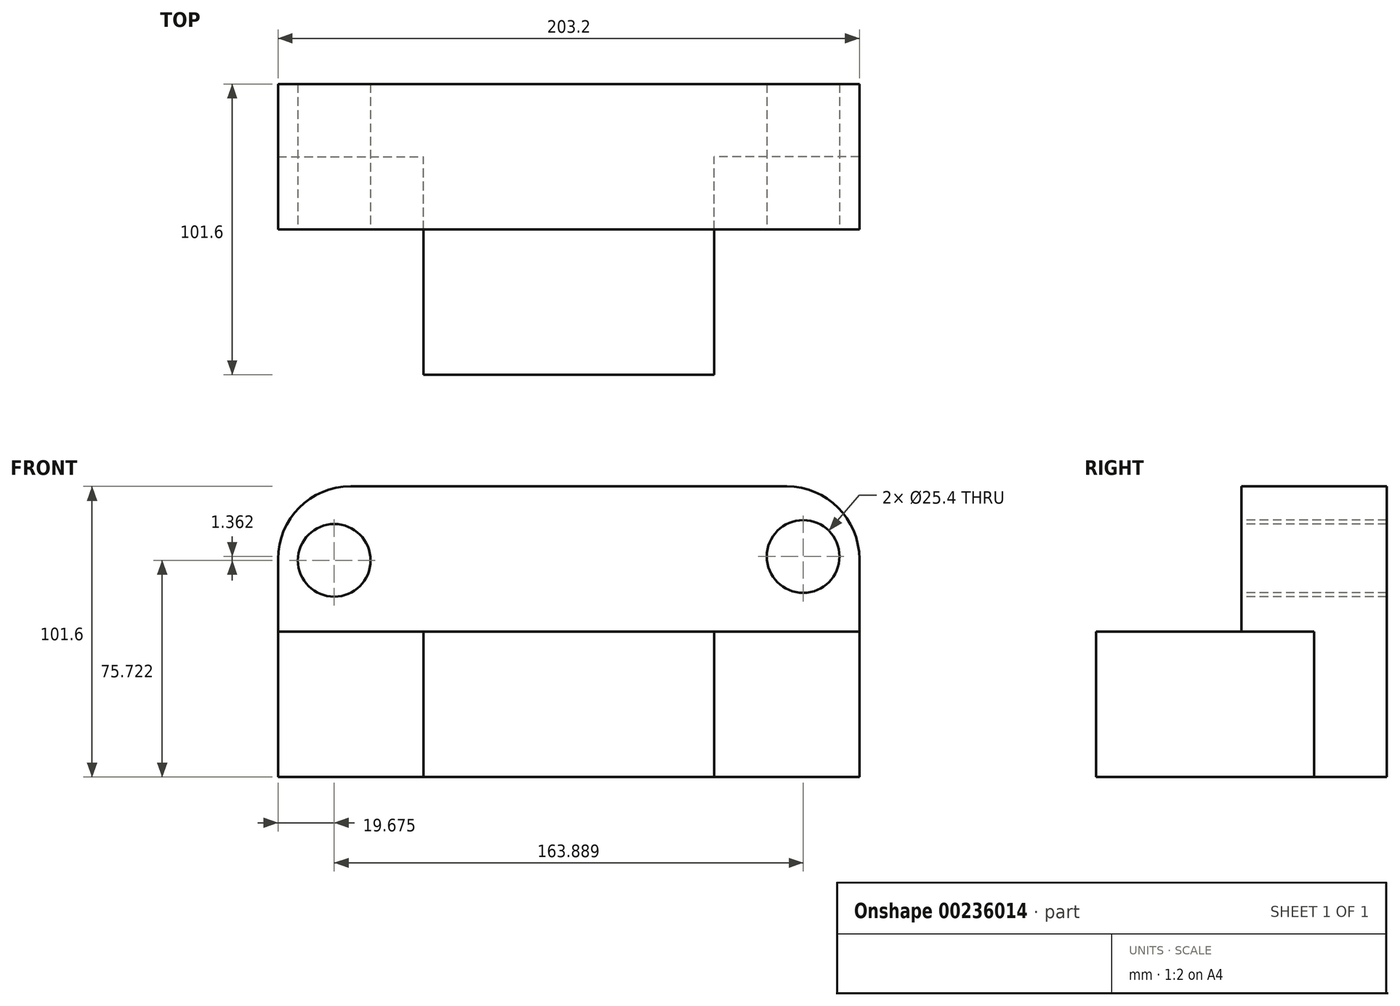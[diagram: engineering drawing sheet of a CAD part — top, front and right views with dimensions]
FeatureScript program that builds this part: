
annotation { "Feature Type Name" : "Feature", "Feature Type Description" : "" }
export const myFeature = defineFeature(function(context is Context, id is Id, definition is map)
    precondition{}
    {
        {
            var Q0;
            Q0=qCreatedBy(makeId("Top.planeOp"),FACE);
            var sketch = newSketch(context, id + "F0", { "sketchPlane" : qUnion([Q0])});
            skLineSegment(sketch, "E0.bottom", {"start": v(-89.89, -22.82) * mm, "end": v(11.71, -22.82) * mm});
            skLineSegment(sketch, "E0.top", {"start": v(-89.89, 78.78) * mm, "end": v(11.71, 78.78) * mm});
            skLineSegment(sketch, "E0.left", {"start": v(-89.89, -22.82) * mm, "end": v(-89.89, 78.78) * mm});
            skLineSegment(sketch, "E0.right", {"start": v(11.71, -22.82) * mm, "end": v(11.71, 78.78) * mm});
            skSolve(sketch);
        }
        {
            var Q0;
            Q0=makeQuery(id+"F0.imprint","IMPRINT",FACE,{"disambiguationData":[TD([[makeQuery(id+"F0.imprint","IMPRINT",EDGE,{"derivedFrom":sQuery(id+"F0.wireOp",EDGE,"E0.bottom")}),1.0]])]});
            extrude(context, id + "F1", {"entities" : qUnion([Q0]), "depth" : 50.8 * mm});
        }
        {
            var Q0;
            Q0=makeQuery(id+"F1.opExtrude","SWEPT_FACE",FACE,{"disambiguationData":[OSD([sQuery(id+"F0.wireOp",EDGE,"E0.right")])]});
            var sketch = newSketch(context, id + "F2", { "sketchPlane" : qUnion([Q0])});
            skLineSegment(sketch, "E1", {"start": v(78.78, 50.8) * mm, "end": v(53.38, 50.8) * mm});
            skLineSegment(sketch, "E2", {"start": v(53.38, 50.8) * mm, "end": v(53.38, 0) * mm});
            skSolve(sketch);
        }
        {
            var Q0;
            Q0=makeQuery(id+"F2.imprint","IMPRINT",FACE,{"disambiguationData":[TD([[makeQuery(id+"F2.imprint","IMPRINT",EDGE,{"derivedFrom":sQuery(id+"F2.wireOp",EDGE,"E1")}),-1.0]])]});
            extrude(context, id + "F3", {"entities" : qUnion([Q0]), "operationType" : NewBodyOperationType.ADD, "depth" : 50.8 * mm});
        }
        {
            var Q0;
            Q0=makeQuery(id+"F1.opExtrude","SWEPT_FACE",FACE,{"disambiguationData":[OSD([sQuery(id+"F0.wireOp",EDGE,"E0.left")])]});
            var sketch = newSketch(context, id + "F4", { "sketchPlane" : qUnion([Q0])});
            skLineSegment(sketch, "E3", {"start": v(-78.78, 50.8) * mm, "end": v(-53.38, 50.8) * mm});
            skLineSegment(sketch, "E4", {"start": v(-53.38, 50.8) * mm, "end": v(-53.38, 0) * mm});
            skSolve(sketch);
        }
        {
            var Q0;
            Q0=makeQuery(id+"F4.imprint","IMPRINT",FACE,{"disambiguationData":[TD([[makeQuery(id+"F4.imprint","IMPRINT",EDGE,{"derivedFrom":sQuery(id+"F4.wireOp",EDGE,"E3")}),1.0]])]});
            extrude(context, id + "F5", {"entities" : qUnion([Q0]), "operationType" : NewBodyOperationType.ADD, "depth" : 50.8 * mm});
        }
        {
            var Q0;
            Q0=makeQuery(id+"F5.boolean.opBoolean","MERGE",FACE,{"derivedFrom":[makeQuery(id+"F3.boolean.opBoolean","MERGE",FACE,{"derivedFrom":[makeQuery(id+"F1.opExtrude","CAP_FACE",FACE,{"disambiguationData":[OSD([sQuery(id+"F0.wireOp",EDGE,"E0.bottom"),sQuery(id+"F0.wireOp",EDGE,"E0.top"),sQuery(id+"F0.wireOp",EDGE,"E0.left"),sQuery(id+"F0.wireOp",EDGE,"E0.right")])],"isStart":false}),makeQuery(id+"F3.opExtrude","SWEPT_FACE",FACE,{"disambiguationData":[OSD([sQuery(id+"F2.wireOp",EDGE,"E1")])]})]}),makeQuery(id+"F5.opExtrude","SWEPT_FACE",FACE,{"disambiguationData":[OSD([sQuery(id+"F4.wireOp",EDGE,"E3")])]})]});
            var sketch = newSketch(context, id + "F6", { "sketchPlane" : qUnion([Q0])});
            skLineSegment(sketch, "E5", {"start": v(-89.89, 53.38) * mm, "end": v(11.71, 53.38) * mm});
            skSolve(sketch);
        }
        {
            var Q0;
            Q0=makeQuery(id+"F6.imprint","IMPRINT",FACE,{"disambiguationData":[TD([[makeQuery(id+"F6.imprint","IMPRINT",EDGE,{"derivedFrom":sQuery(id+"F6.wireOp",EDGE,"E5")}),1.0]])]});
            extrude(context, id + "F7", {"entities" : qUnion([Q0]), "operationType" : NewBodyOperationType.ADD, "depth" : 25.4 * mm});
        }
        {
            var Q0;
            Q0=makeQuery(id+"F7.opExtrude","CAP_FACE",FACE,{"disambiguationData":[OSD([sQuery(id+"F0.wireOp",EDGE,"E0.top"),sQuery(id+"F0.wireOp",EDGE,"E0.left"),sQuery(id+"F0.wireOp",EDGE,"E0.right"),sQuery(id+"F2.wireOp",EDGE,"E1"),sQuery(id+"F2.wireOp",EDGE,"E2"),sQuery(id+"F4.wireOp",EDGE,"E3"),sQuery(id+"F4.wireOp",EDGE,"E4"),sQuery(id+"F6.wireOp",EDGE,"E5")])],"isStart":false});
            extrude(context, id + "F8", {"entities" : qUnion([Q0]), "operationType" : NewBodyOperationType.ADD, "depth" : 25.4 * mm});
        }
        {
            var Q0;
            {var subQ0=sQuery(id+"F6.wireOp",EDGE,"E5");var subQ1=sQuery(id+"F4.wireOp",EDGE,"E4");var subQ2=sQuery(id+"F4.wireOp",EDGE,"E3");var subQ3=sQuery(id+"F2.wireOp",EDGE,"E2");var subQ4=sQuery(id+"F2.wireOp",EDGE,"E1");var subQ5=sQuery(id+"F0.wireOp",EDGE,"E0.right");var subQ6=sQuery(id+"F0.wireOp",EDGE,"E0.left");Q0=makeQuery(id+"F8.boolean.opBoolean","MERGE",FACE,{"derivedFrom":[makeQuery(id+"F7.boolean.opBoolean","MERGE",FACE,{"derivedFrom":[makeQuery(id+"F3.opExtrude","SWEPT_FACE",FACE,{"disambiguationData":[OSD([subQ3])]}),makeQuery(id+"F5.opExtrude","SWEPT_FACE",FACE,{"disambiguationData":[OSD([subQ1])]}),makeQuery(id+"F7.opExtrude","SWEPT_FACE",FACE,{"disambiguationData":[OSD([subQ6,subQ5,subQ4,subQ3,subQ2,subQ1,subQ0])]})]}),makeQuery(id+"F8.opExtrude","SWEPT_FACE",FACE,{"disambiguationData":[OSD([subQ6,subQ5,subQ4,subQ3,subQ2,subQ1,subQ0])]})]});}
            var sketch = newSketch(context, id + "F9", { "sketchPlane" : qUnion([Q0])});
            skLineSegment(sketch, "E6", {"start": v(-89.89, 50.8) * mm, "end": v(-140.69, 50.8) * mm});
            skLineSegment(sketch, "E7", {"start": v(11.71, 50.8) * mm, "end": v(62.51, 50.8) * mm});
            skSolve(sketch);
        }
        {
            var Q0;
            {var subQ9=sQuery(id+"F9.wireOp",EDGE,"E6");Q0=makeQuery(id+"F9.imprint","IMPRINT",FACE,{"disambiguationData":[TD([[makeQuery(id+"F9.imprint","IMPRINT",EDGE,{"derivedFrom":subQ9}),-1.0]])]});}
            extrude(context, id + "F10", {"entities" : qUnion([Q0]), "operationType" : NewBodyOperationType.ADD, "depth" : 25.4 * mm});
        }
        {
            var Q0;
            Q0=makeQuery(id+"F10.opExtrude","CAP_FACE",FACE,{"disambiguationData":[OSD([sQuery(id+"F0.wireOp",EDGE,"E0.left"),sQuery(id+"F0.wireOp",EDGE,"E0.right"),sQuery(id+"F2.wireOp",EDGE,"E1"),sQuery(id+"F2.wireOp",EDGE,"E2"),sQuery(id+"F4.wireOp",EDGE,"E3"),sQuery(id+"F4.wireOp",EDGE,"E4"),sQuery(id+"F6.wireOp",EDGE,"E5"),sQuery(id+"F9.wireOp",EDGE,"E6"),sQuery(id+"F9.wireOp",EDGE,"E7")])],"isStart":false});
            var sketch = newSketch(context, id + "F11", { "sketchPlane" : qUnion([Q0])});
            skCircle(sketch, "E8", {"center": v(31.18, 80.79) * mm, "radius": 12.7 * mm});
            skCircle(sketch, "E9", {"center": v(-121.02, 75.72) * mm, "radius": 12.7 * mm});
            skSolve(sketch);
        }
        {
            var Q0;
            Q0=makeQuery(id+"F11.imprint","IMPRINT",FACE,{"disambiguationData":[TD([[makeQuery(id+"F11.imprint","IMPRINT",EDGE,{"derivedFrom":sQuery(id+"F11.wireOp",EDGE,"E9")}),1.0]])]});
            extrude(context, id + "F12", {"entities" : qUnion([Q0]), "operationType" : NewBodyOperationType.REMOVE, "oppositeDirection" : true, "depth" : 50.8 * mm});
        }
        {
            var Q0;
            Q0=makeQuery(id+"F10.opExtrude","CAP_FACE",FACE,{"disambiguationData":[OSD([sQuery(id+"F0.wireOp",EDGE,"E0.left"),sQuery(id+"F0.wireOp",EDGE,"E0.right"),sQuery(id+"F2.wireOp",EDGE,"E1"),sQuery(id+"F2.wireOp",EDGE,"E2"),sQuery(id+"F4.wireOp",EDGE,"E3"),sQuery(id+"F4.wireOp",EDGE,"E4"),sQuery(id+"F6.wireOp",EDGE,"E5"),sQuery(id+"F9.wireOp",EDGE,"E6"),sQuery(id+"F9.wireOp",EDGE,"E7")])],"isStart":false});
            var sketch = newSketch(context, id + "F13", { "sketchPlane" : qUnion([Q0])});
            skLineSegment(sketch, "E10", {"start": v(-140.69, 76.2) * mm, "end": v(-121.02, 75.72) * mm});
            skLineSegment(sketch, "E11", {"start": v(62.51, 75.72) * mm, "end": v(42.87, 77.08) * mm});
            skCircle(sketch, "E12", {"center": v(42.87, 77.08) * mm, "radius": 12.7 * mm});
            skSolve(sketch);
        }
        {
            var Q0;
            Q0=makeQuery(id+"F13.imprint","IMPRINT",FACE,{"disambiguationData":[TD([[makeQuery(id+"F13.imprint","IMPRINT",EDGE,{"derivedFrom":sQuery(id+"F13.wireOp",EDGE,"E12")}),1.0]])]});
            extrude(context, id + "F14", {"entities" : qUnion([Q0]), "operationType" : NewBodyOperationType.REMOVE, "oppositeDirection" : true, "depth" : 50.8 * mm});
        }
        {
            var Q0;
            {var subQ0=sQuery(id+"F2.wireOp",EDGE,"E2");var subQ1=sQuery(id+"F2.wireOp",EDGE,"E1");var subQ2=sQuery(id+"F0.wireOp",EDGE,"E0.right");var subQ3=sQuery(id+"F6.wireOp",EDGE,"E5");var subQ4=sQuery(id+"F4.wireOp",EDGE,"E4");var subQ5=sQuery(id+"F4.wireOp",EDGE,"E3");var subQ6=sQuery(id+"F0.wireOp",EDGE,"E0.left");Q0=makeQuery(id+"F10.boolean.opBoolean","MERGE",EDGE,{"derivedFrom":[makeQuery(id+"F8.opExtrude","CAP_EDGE",EDGE,{"disambiguationData":[OSD([subQ1])],"isStart":false}),makeQuery(id+"F10.opExtrude","SWEPT_EDGE",EDGE,{"disambiguationData":[OSD([subQ6,subQ2,subQ1,subQ0,subQ5,subQ4,subQ3]),TDD([makeQuery(id+"F9.imprint","INTERSECT",VERTEX,{"derivedFrom":[makeQuery(id+"F8.opExtrude","CAP_EDGE",EDGE,{"disambiguationData":[OSD([subQ6,subQ2,subQ1,subQ0,subQ5,subQ4,subQ3])],"isStart":false}),makeQuery(id+"F8.boolean.opBoolean","MERGE",EDGE,{"derivedFrom":[makeQuery(id+"F7.boolean.opBoolean","MERGE",EDGE,{"derivedFrom":[makeQuery(id+"F3.opExtrude","CAP_EDGE",EDGE,{"disambiguationData":[OSD([subQ0])],"isStart":false}),makeQuery(id+"F7.opExtrude","SWEPT_EDGE",EDGE,{"disambiguationData":[OSD([subQ2,subQ1,subQ0])]})]}),makeQuery(id+"F8.opExtrude","SWEPT_EDGE",EDGE,{"disambiguationData":[OSD([subQ2,subQ1,subQ0])]})]})]})])]})]});}
            fillet(context, id + "F15", {"entities" : qUnion([Q0]), "radius" : 25.4 * mm, "tangentPropagation" : true, "allowEdgeOverflow" : false});
        }
        {
            var Q0;
            {var subQ0=sQuery(id+"F4.wireOp",EDGE,"E4");var subQ1=sQuery(id+"F4.wireOp",EDGE,"E3");var subQ2=sQuery(id+"F0.wireOp",EDGE,"E0.left");var subQ3=sQuery(id+"F6.wireOp",EDGE,"E5");var subQ4=sQuery(id+"F2.wireOp",EDGE,"E2");var subQ5=sQuery(id+"F2.wireOp",EDGE,"E1");var subQ6=sQuery(id+"F0.wireOp",EDGE,"E0.right");Q0=makeQuery(id+"F10.boolean.opBoolean","MERGE",EDGE,{"derivedFrom":[makeQuery(id+"F8.opExtrude","CAP_EDGE",EDGE,{"disambiguationData":[OSD([subQ1])],"isStart":false}),makeQuery(id+"F10.opExtrude","SWEPT_EDGE",EDGE,{"disambiguationData":[OSD([subQ2,subQ6,subQ5,subQ4,subQ1,subQ0,subQ3]),TDD([makeQuery(id+"F9.imprint","INTERSECT",VERTEX,{"derivedFrom":[makeQuery(id+"F8.opExtrude","CAP_EDGE",EDGE,{"disambiguationData":[OSD([subQ2,subQ6,subQ5,subQ4,subQ1,subQ0,subQ3])],"isStart":false}),makeQuery(id+"F8.boolean.opBoolean","MERGE",EDGE,{"derivedFrom":[makeQuery(id+"F7.boolean.opBoolean","MERGE",EDGE,{"derivedFrom":[makeQuery(id+"F5.opExtrude","CAP_EDGE",EDGE,{"disambiguationData":[OSD([subQ0])],"isStart":false}),makeQuery(id+"F7.opExtrude","SWEPT_EDGE",EDGE,{"disambiguationData":[OSD([subQ2,subQ1,subQ0])]})]}),makeQuery(id+"F8.opExtrude","SWEPT_EDGE",EDGE,{"disambiguationData":[OSD([subQ2,subQ1,subQ0])]})]})]})])]})]});}
            fillet(context, id + "F16", {"entities" : qUnion([Q0]), "radius" : 25.4 * mm, "tangentPropagation" : true, "allowEdgeOverflow" : false});
        }
    });
